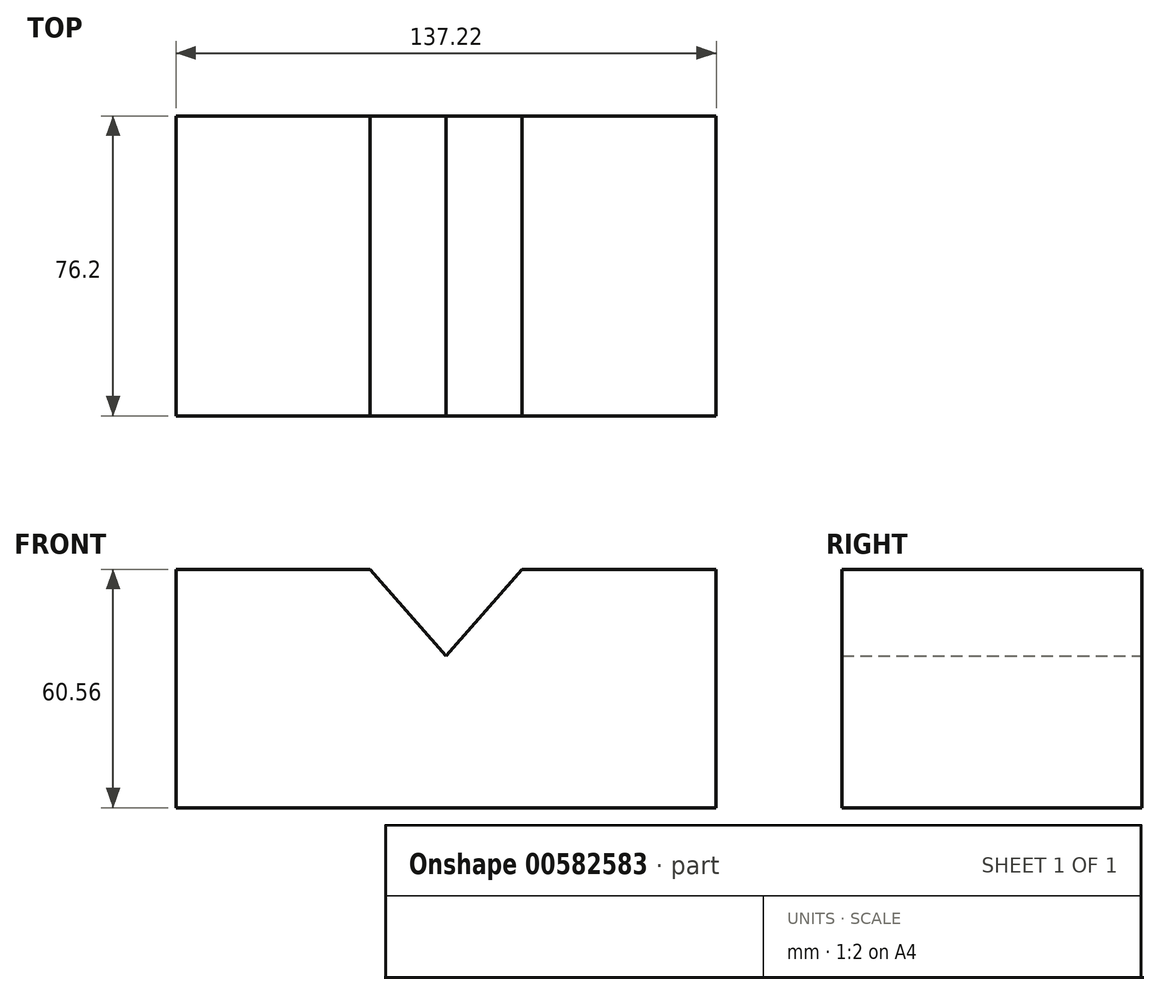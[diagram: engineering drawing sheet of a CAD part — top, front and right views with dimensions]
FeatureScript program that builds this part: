
annotation { "Feature Type Name" : "Feature", "Feature Type Description" : "" }
export const myFeature = defineFeature(function(context is Context, id is Id, definition is map)
    precondition{}
    {
        {
            var Q0;
            Q0=qCreatedBy(makeId("Front.planeOp"),FACE);
            var sketch = newSketch(context, id + "F0", { "sketchPlane" : qUnion([Q0])});
            skLineSegment(sketch, "E0.bottom", {"start": v(68.6, 60.56) * mm, "end": v(19.3, 60.56) * mm});
            skLineSegment(sketch, "E0.top", {"start": v(68.6, 0) * mm, "end": v(0, 0) * mm});
            skLineSegment(sketch, "E0.left", {"start": v(68.6, 60.56) * mm, "end": v(68.6, 0) * mm});
            skLineSegment(sketch, "E0.right", {"start": v(0, 38.56) * mm, "end": v(0, 0) * mm});
            skLineSegment(sketch, "E1", {"start": v(0, 38.56) * mm, "end": v(19.3, 60.56) * mm});
            skLineSegment(sketch, "E2.MirrorCS", {"start": v(-68.6, 0) * mm, "end": v(0, 0) * mm});
            skLineSegment(sketch, "E3.MirrorCS", {"start": v(-68.6, 60.56) * mm, "end": v(-68.6, 0) * mm});
            skLineSegment(sketch, "E4.MirrorCS", {"start": v(-68.6, 60.56) * mm, "end": v(-19.3, 60.56) * mm});
            skLineSegment(sketch, "E5.MirrorCS", {"start": v(0, 38.56) * mm, "end": v(-19.3, 60.56) * mm});
            skSolve(sketch);
        }
        {
            var Q0;
            Q0=makeQuery(id+"F0.imprint","IMPRINT",FACE,{"disambiguationData":[TD([[makeQuery(id+"F0.imprint","IMPRINT",EDGE,{"derivedFrom":sQuery(id+"F0.wireOp",EDGE,"E0.right")}),-1.0]])]});
            var Q1;
            Q1=makeQuery(id+"F0.imprint","IMPRINT",FACE,{"disambiguationData":[TD([[makeQuery(id+"F0.imprint","IMPRINT",EDGE,{"derivedFrom":sQuery(id+"F0.wireOp",EDGE,"E0.bottom")}),1.0]])]});
            extrude(context, id + "F1", {"entities" : qUnion([Q0, Q1]), "depth" : 76.2 * mm, "offsetDistance" : 25.4 * mm});
        }
    });
